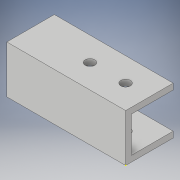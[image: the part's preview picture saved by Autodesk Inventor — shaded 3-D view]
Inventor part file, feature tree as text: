
AUTODESK INVENTOR PART (.ipt)
format: ipt  version: 2018 (Build 220112000, 112)  size: 123,392 bytes
history: native  units: in
note: dims shown in document units (in); Inventor stores cm internally (conversion verified against a paired STEP export)
features: extrude x3, sketch x3, projected_geometry x1
ambient origin geometry x8: Origin, YZ Plane, XZ Plane, XY Plane, X Axis, Y Axis, Z Axis, Center Point
bodies: Solid1 (feature_tree)
feature tree (7):
  extrude  "Extrusion1"  Depth=1.0in
  sketch  "Sketch2"  dims[d2=1.0in d3=0.0in d4=0.125in]
  extrude  "Extrusion3"  Depth=0.125in
  extrude  "Extrusion4"  Depth=0.75in
  sketch  "Sketch1"  dims[d0=2.5in d1=1.0in]
  projected_geometry  "Projected Loop1"
  sketch  "Sketch4"  dims[d7=0.5in d8=0.75in d9=0.2031in d10=0.2031in d11=2.5in d12=0.0in d13=5.0in d14=0.0in]
